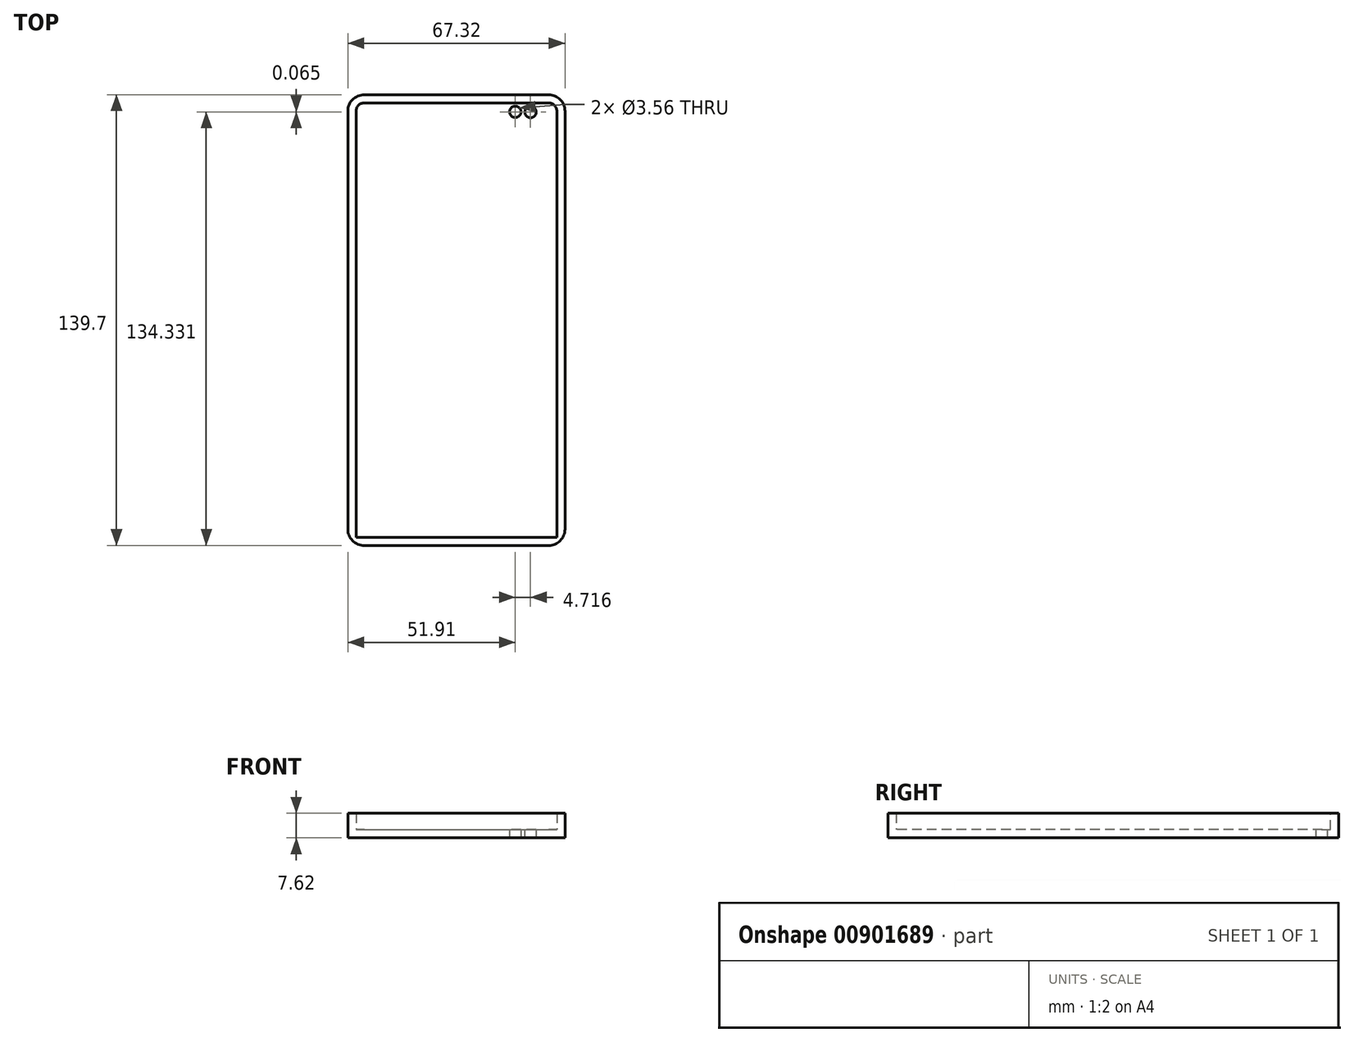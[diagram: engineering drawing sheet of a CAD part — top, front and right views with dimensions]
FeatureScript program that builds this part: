
annotation { "Feature Type Name" : "Feature", "Feature Type Description" : "" }
export const myFeature = defineFeature(function(context is Context, id is Id, definition is map)
    precondition{}
    {
        {
            var Q0;
            Q0=qCreatedBy(makeId("Top.planeOp"),FACE);
            var sketch = newSketch(context, id + "F0", { "sketchPlane" : qUnion([Q0])});
            skLineSegment(sketch, "E0.bottom", {"start": v(-33.65, 69.85) * mm, "end": v(33.66, 69.85) * mm});
            skLineSegment(sketch, "E0.top", {"start": v(-33.66, -69.85) * mm, "end": v(33.65, -69.85) * mm});
            skLineSegment(sketch, "E0.left", {"start": v(-33.65, 69.85) * mm, "end": v(-33.66, -69.85) * mm});
            skLineSegment(sketch, "E0.right", {"start": v(33.66, 69.85) * mm, "end": v(33.65, -69.85) * mm});
            skPoint(sketch, "E0.middle", {"position": v(0, 0) * mm});
            skSolve(sketch);
        }
        {
            var Q0;
            Q0=makeQuery(id+"F0.imprint","IMPRINT",FACE,{"disambiguationData":[TD([[makeQuery(id+"F0.imprint","IMPRINT",EDGE,{"derivedFrom":sQuery(id+"F0.wireOp",EDGE,"E0.bottom")}),-1.0]])]});
            extrude(context, id + "F1", {"entities" : qUnion([Q0]), "depth" : 7.62 * mm, "offsetDistance" : 25.4 * mm});
        }
        {
            var Q0;
            Q0=makeQuery(id+"F1.opExtrude","SWEPT_EDGE",EDGE,{"disambiguationData":[OSD([sQuery(id+"F0.wireOp",EDGE,"E0.bottom"),sQuery(id+"F0.wireOp",EDGE,"E0.right")])]});
            var Q1;
            Q1=makeQuery(id+"F1.opExtrude","SWEPT_EDGE",EDGE,{"disambiguationData":[OSD([sQuery(id+"F0.wireOp",EDGE,"E0.bottom"),sQuery(id+"F0.wireOp",EDGE,"E0.left")])]});
            fillet(context, id + "F2", {"entities" : qUnion([Q0, Q1]), "radius" : 5.08 * mm, "tangentPropagation" : true, "allowEdgeOverflow" : false});
        }
        {
            var Q0;
            Q0=makeQuery(id+"F1.opExtrude","CAP_FACE",FACE,{"disambiguationData":[OSD([sQuery(id+"F0.wireOp",EDGE,"E0.bottom"),sQuery(id+"F0.wireOp",EDGE,"E0.top"),sQuery(id+"F0.wireOp",EDGE,"E0.left"),sQuery(id+"F0.wireOp",EDGE,"E0.right")])],"isStart":false});
            shell(context, id + "F3", {"entities" : qUnion([Q0]), "thickness" : 2.54 * mm});
        }
        {
            var Q0;
            Q0=makeQuery(id+"F1.opExtrude","SWEPT_EDGE",EDGE,{"disambiguationData":[OSD([sQuery(id+"F0.wireOp",EDGE,"E0.top"),sQuery(id+"F0.wireOp",EDGE,"E0.left")])]});
            fillet(context, id + "F4", {"entities" : qUnion([Q0]), "radius" : 5.08 * mm, "tangentPropagation" : true, "allowEdgeOverflow" : false});
        }
        {
            var Q0;
            Q0=makeQuery(id+"F0.imprint","IMPRINT",FACE,{"disambiguationData":[TD([[makeQuery(id+"F0.imprint","IMPRINT",EDGE,{"derivedFrom":sQuery(id+"F0.wireOp",EDGE,"E0.bottom")}),-1.0]])]});
            var sketch = newSketch(context, id + "F5", { "sketchPlane" : qUnion([Q0])});
            skCircle(sketch, "E1", {"center": v(22.97, 64.48) * mm, "radius": 1.9 * mm});
            skCircle(sketch, "E2", {"center": v(18.25, 64.55) * mm, "radius": 1.9 * mm});
            skSolve(sketch);
        }
        {
            var Q0;
            Q0=makeQuery(id+"F1.opExtrude","SWEPT_EDGE",EDGE,{"disambiguationData":[OSD([sQuery(id+"F0.wireOp",EDGE,"E0.top"),sQuery(id+"F0.wireOp",EDGE,"E0.right")])]});
            fillet(context, id + "F6", {"entities" : qUnion([Q0]), "radius" : 5.08 * mm, "tangentPropagation" : true, "allowEdgeOverflow" : false});
        }
        {
            var Q0;
            Q0=sQuery(id+"F5.wireOp",VERTEX,"E2.center");
            var Q1;
            Q1=makeQuery(id+"F1.opExtrude","SWEPT_BODY",BODY,{"disambiguationData":[OSD([sQuery(id+"F0.wireOp",EDGE,"E0.bottom"),sQuery(id+"F0.wireOp",EDGE,"E0.top"),sQuery(id+"F0.wireOp",EDGE,"E0.left"),sQuery(id+"F0.wireOp",EDGE,"E0.right")])]});
            hole(context, id + "F7", {"style" : HoleStyle.SIMPLE, "endStyle" : HoleEndStyle.THROUGH, "oppositeDirection" : true, "holeDiameter" : 3.56 * mm, "majorDiameter" : 6.35 * mm, "isTappedThrough" : true, "tappedDepth" : 12.7 * mm, "tapClearance" : 3, "locations" : qUnion([Q0]), "scope" : qUnion([Q1])});
        }
        {
            var Q0;
            Q0=sQuery(id+"F5.wireOp",VERTEX,"E1.center");
            var Q1;
            Q1=makeQuery(id+"F1.opExtrude","SWEPT_BODY",BODY,{"disambiguationData":[OSD([sQuery(id+"F0.wireOp",EDGE,"E0.bottom"),sQuery(id+"F0.wireOp",EDGE,"E0.top"),sQuery(id+"F0.wireOp",EDGE,"E0.left"),sQuery(id+"F0.wireOp",EDGE,"E0.right")])]});
            hole(context, id + "F8", {"style" : HoleStyle.SIMPLE, "endStyle" : HoleEndStyle.THROUGH, "oppositeDirection" : true, "holeDiameter" : 3.56 * mm, "majorDiameter" : 6.35 * mm, "isTappedThrough" : true, "tappedDepth" : 12.7 * mm, "tapClearance" : 3, "locations" : qUnion([Q0]), "scope" : qUnion([Q1])});
        }
    });
